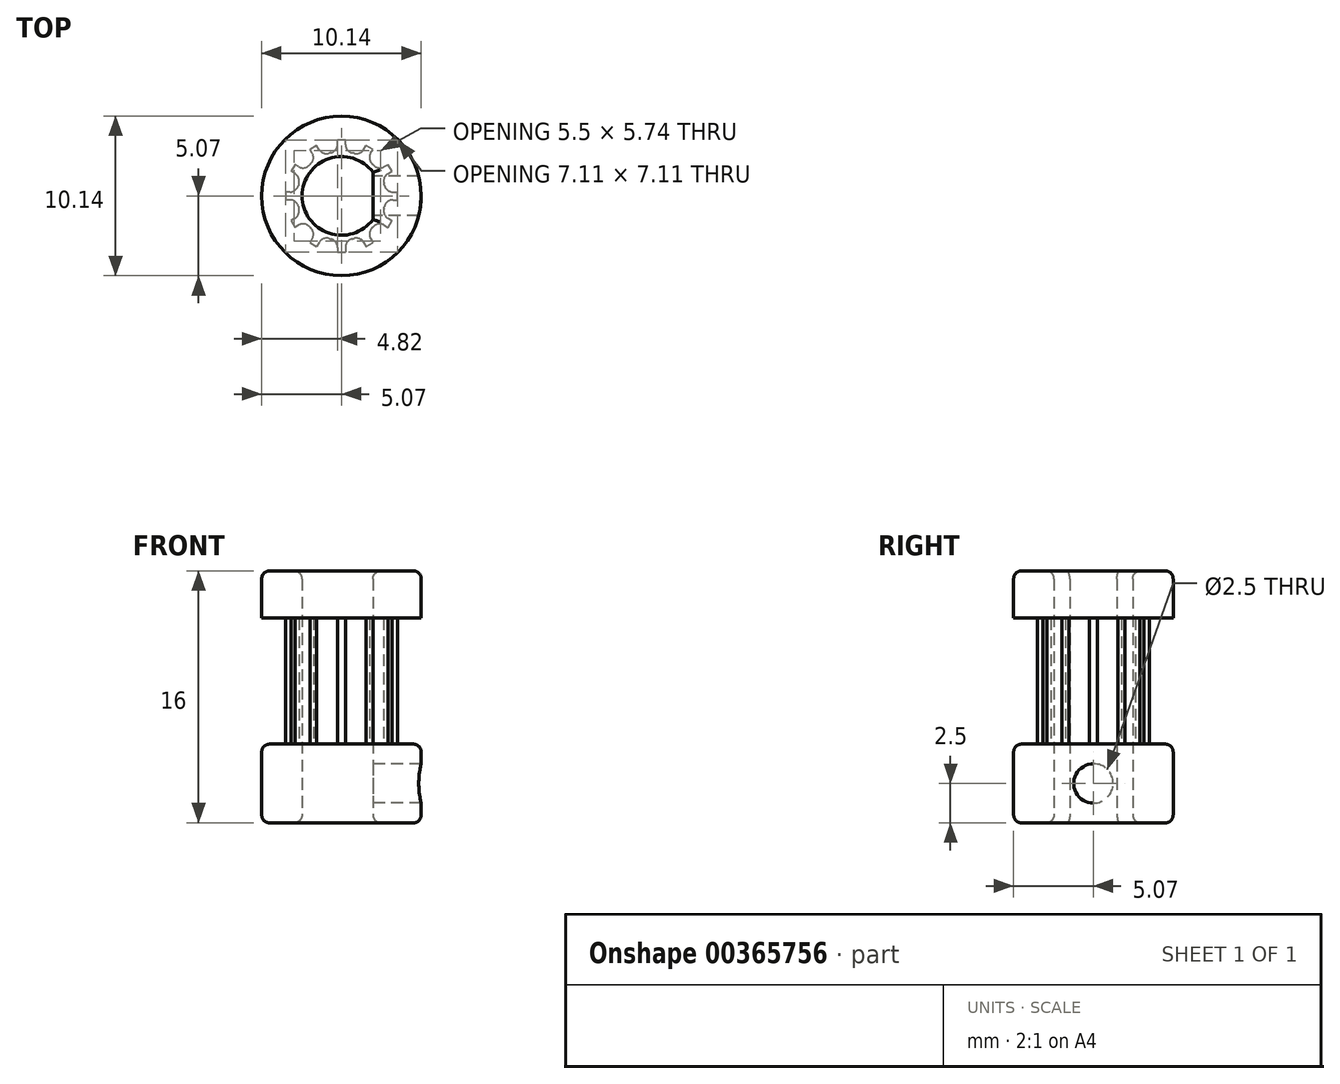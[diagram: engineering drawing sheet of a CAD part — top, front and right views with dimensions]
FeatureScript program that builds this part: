
annotation { "Feature Type Name" : "Feature", "Feature Type Description" : "" }
export const myFeature = defineFeature(function(context is Context, id is Id, definition is map)
    precondition{}
    {
        {
            assignVariable(context, id + "F0", {"name" : "Pulley_height", "anyValue" : 16});
        }
        {
            assignVariable(context, id + "F1", {"name" : "Belt_width", "anyValue" : 8});
        }
        {
            assignVariable(context, id + "F2", {"name" : "Nr_of_teeth", "anyValue" : 12});
        }
        {
            assignVariable(context, id + "F3", {"name" : "Top_sleeve_thickness", "anyValue" : 3});
        }
        {
            var Q0;
            Q0=qCreatedBy(makeId("Top.planeOp"),FACE);
            var sketch = newSketch(context, id + "F4", { "sketchPlane" : qUnion([Q0])});
            skCircle(sketch, "E0", {"center": v(0, 0) * mm, "radius": 3.57 * mm, "construction": true});
            skCircle(sketch, "E1", {"center": v(0, 0) * mm, "radius": 5.07 * mm});
            skLineSegment(sketch, "E2", {"start": v(0, -3.57) * mm, "end": v(0, 0) * mm, "construction": true});
            skLineSegment(sketch, "E3.bottom", {"start": v(-0.25, -2.8) * mm, "end": v(0.25, -2.8) * mm});
            skLineSegment(sketch, "E3.top", {"start": v(-0.25, -3.56) * mm, "end": v(0.25, -3.56) * mm});
            skLineSegment(sketch, "E3.left", {"start": v(-0.25, -3.27) * mm, "end": v(-0.25, -3.56) * mm});
            skLineSegment(sketch, "E3.right", {"start": v(0.25, -3.27) * mm, "end": v(0.25, -3.56) * mm});
            skPoint(sketch, "E3.middle", {"position": v(0, -3.18) * mm});
            skArc(sketch, "E4", {"start": v(0.67, -2.74) * mm, "mid": v(-0.21, 2.8) * mm, "end": v(-0.25, -2.8) * mm});
            skPoint(sketch, "E5.visualSharp", {"position": v(0.25, -2.8) * mm});
            skArc(sketch, "E5.filletArc", {"start": v(0.67, -2.74) * mm, "mid": v(0.37, -2.93) * mm, "end": v(0.25, -3.27) * mm});
            skArc(sketch, "E6.MirrorCS", {"start": v(-0.67, -2.74) * mm, "mid": v(-0.37, -2.93) * mm, "end": v(-0.25, -3.27) * mm});
            skLineSegment(sketch, "E7", {"start": v(0.67, -2.74) * mm, "end": v(0.25, -2.8) * mm});
            skCircle(sketch, "E8", {"center": v(0, 0) * mm, "radius": 2.5 * mm});
            skLineSegment(sketch, "E9", {"start": v(2, -1.5) * mm, "end": v(2, 1.5) * mm});
            skSolve(sketch);
        }
        {
            var Q0;
            {var subQ3=sQuery(id+"F4.wireOp",EDGE,"E3.bottom");Q0=makeQuery(id+"F4.imprint","IMPRINT",FACE,{"disambiguationData":[TD([[makeQuery(id+"F4.imprint","IMPRINT",EDGE,{"derivedFrom":subQ3}),1.0]])]});}
            var Q1;
            {var subQ0=sQuery(id+"F4.wireOp",EDGE,"c6fd6b1b-5dc8-40e9-8271-47284b0c1c390.MirrorCS");Q1=makeQuery(id+"F4.imprint","IMPRINT",FACE,{"disambiguationData":[TD([[makeQuery(id+"F4.imprint","IMPRINT",EDGE,{"derivedFrom":subQ0}),1.0]])]});}
            var Q2;
            {var subQ0=sQuery(id+"F4.wireOp",EDGE,"E9");Q2=makeQuery(id+"F4.imprint","IMPRINT",FACE,{"disambiguationData":[TD([[makeQuery(id+"F4.imprint","IMPRINT",EDGE,{"derivedFrom":subQ0}),-1.0]])]});}
            var Q3;
            Q3=makeQuery(id+"F4.imprint","IMPRINT",FACE,{"disambiguationData":[TD([[makeQuery(id+"F4.imprint","IMPRINT",EDGE,{"derivedFrom":sQuery(id+"F4.wireOp",EDGE,"E1")}),1.0]])]});
            var Q4;
            {var subQ0=sQuery(id+"F4.wireOp",EDGE,"E3.bottom");Q4=makeQuery(id+"F4.imprint","IMPRINT",FACE,{"disambiguationData":[TD([[makeQuery(id+"F4.imprint","IMPRINT",EDGE,{"derivedFrom":subQ0}),-1.0]])]});}
            extrude(context, id + "F5", {"entities" : qUnion([Q0, Q1, Q2, Q3, Q4]), "depth" : (getVariable(context, 'Pulley_height')) * mm});
        }
        {
            var Q0;
            Q0=makeQuery(id+"F4.imprint","IMPRINT",FACE,{"disambiguationData":[TD([[makeQuery(id+"F4.imprint","IMPRINT",EDGE,{"derivedFrom":sQuery(id+"F4.wireOp",EDGE,"E1")}),1.0]])]});
            var Q1;
            Q1=sQuery(id+"F4.wireOp",EDGE,"E1");
            extrude(context, id + "F6", {"entities" : qUnion([Q0]), "operationType" : NewBodyOperationType.REMOVE, "surfaceEntities" : qUnion([Q1]), "depth" : (getVariable(context, 'Pulley_height') - getVariable(context, 'Top_sleeve_thickness')) * mm});
        }
        {
            var Q0;
            Q0=makeQuery(id+"F4.imprint","IMPRINT",FACE,{"disambiguationData":[TD([[makeQuery(id+"F4.imprint","IMPRINT",EDGE,{"derivedFrom":sQuery(id+"F4.wireOp",EDGE,"E1")}),1.0]])]});
            extrude(context, id + "F7", {"entities" : qUnion([Q0]), "operationType" : NewBodyOperationType.ADD, "depth" : (getVariable(context, 'Pulley_height') - getVariable(context, 'Top_sleeve_thickness') - getVariable(context, 'Belt_width')) * mm});
        }
        {
            var Q0;
            Q0=qCreatedBy(makeId("Right.planeOp"),FACE);
            var sketch = newSketch(context, id + "F8", { "sketchPlane" : qUnion([Q0])});
            skCircle(sketch, "E10", {"center": v(0, 2.5) * mm, "radius": 1.25 * mm});
            skLineSegment(sketch, "E11", {"start": v(0, 0) * mm, "end": v(0, 16.5) * mm, "construction": true});
            skSolve(sketch);
        }
        {
            var Q0;
            Q0=makeQuery(id+"F8.imprint","IMPRINT",FACE,{"disambiguationData":[TD([[makeQuery(id+"F8.imprint","IMPRINT",EDGE,{"derivedFrom":sQuery(id+"F8.wireOp",EDGE,"E10")}),1.0]])]});
            var Q1;
            Q1=sQuery(id+"F8.wireOp",EDGE,"E10");
            extrude(context, id + "F9", {"entities" : qUnion([Q0]), "operationType" : NewBodyOperationType.REMOVE, "surfaceEntities" : qUnion([Q1]), "endBound" : BoundingType.THROUGH_ALL, "depth" : 25 * mm});
        }
        {
            var Q0;
            Q0=makeQuery(id+"F6.boolean.opBoolean","COPY",FACE,{"derivedFrom":makeQuery(id+"F6.opExtrude","SWEPT_FACE",FACE,{"disambiguationData":[OSD([sQuery(id+"F4.wireOp",EDGE,"E3.top")])]})});
            var Q1;
            Q1=makeQuery(id+"F6.boolean.opBoolean","COPY",FACE,{"derivedFrom":makeQuery(id+"F6.opExtrude","SWEPT_FACE",FACE,{"disambiguationData":[OSD([sQuery(id+"F4.wireOp",EDGE,"E6.MirrorCS")])]})});
            var Q2;
            Q2=makeQuery(id+"F6.boolean.opBoolean","COPY",FACE,{"derivedFrom":makeQuery(id+"F6.opExtrude","SWEPT_FACE",FACE,{"disambiguationData":[OSD([sQuery(id+"F4.wireOp",EDGE,"E5.filletArc")])]})});
            var Q3;
            Q3=makeQuery(id+"F6.boolean.opBoolean","COPY",FACE,{"derivedFrom":makeQuery(id+"F6.opExtrude","SWEPT_FACE",FACE,{"disambiguationData":[OSD([sQuery(id+"F4.wireOp",EDGE,"E3.left")])]})});
            var Q4;
            Q4=makeQuery(id+"F6.boolean.opBoolean","COPY",FACE,{"derivedFrom":makeQuery(id+"F6.opExtrude","SWEPT_FACE",FACE,{"disambiguationData":[OSD([sQuery(id+"F4.wireOp",EDGE,"E3.right")])]})});
            var Q5;
            Q5=sQuery(id+"F8.wireOp",EDGE,"E11");
            circularPattern(context, id + "F10", {"patternType" : PatternType.FACE, "operationType" : NewBodyOperationType.ADD, "faces" : qUnion([Q0, Q1, Q2, Q3, Q4]), "axis" : qUnion([Q5]), "angle" : 360 * degree, "instanceCount" : getVariable(context, 'Nr_of_teeth'), "equalSpace" : true});
        }
        {
            var Q0;
            Q0=makeQuery(id+"F6.boolean.opBoolean","COPY",EDGE,{"derivedFrom":makeQuery(id+"F6.opExtrude","CAP_EDGE",EDGE,{"disambiguationData":[OSD([sQuery(id+"F4.wireOp",EDGE,"E1")])],"isStart":false})});
            var Q1;
            Q1=makeQuery(id+"F5.opExtrude","CAP_EDGE",EDGE,{"disambiguationData":[OSD([sQuery(id+"F4.wireOp",EDGE,"E1")])],"isStart":false});
            var Q2;
            Q2=makeQuery(id+"F7.opExtrude","CAP_EDGE",EDGE,{"disambiguationData":[OSD([sQuery(id+"F4.wireOp",EDGE,"E1")])],"isStart":false});
            var Q3;
            Q3=makeQuery(id+"F7.opExtrude","CAP_EDGE",EDGE,{"disambiguationData":[OSD([sQuery(id+"F4.wireOp",EDGE,"E1")])],"isStart":true});
            var Q4;
            Q4=makeQuery(id+"F5.opExtrude","CAP_EDGE",EDGE,{"disambiguationData":[OSD([sQuery(id+"F4.wireOp",EDGE,"E8")])],"isStart":false});
            var Q5;
            Q5=makeQuery(id+"F5.opExtrude","CAP_EDGE",EDGE,{"disambiguationData":[OSD([sQuery(id+"F4.wireOp",EDGE,"E8")])],"isStart":true});
            var Q6;
            Q6=makeQuery(id+"F5.opExtrude","CAP_EDGE",EDGE,{"disambiguationData":[OSD([sQuery(id+"F4.wireOp",EDGE,"E9")])],"isStart":true});
            var Q7;
            Q7=makeQuery(id+"F5.opExtrude","CAP_EDGE",EDGE,{"disambiguationData":[OSD([sQuery(id+"F4.wireOp",EDGE,"E9")])],"isStart":false});
            fillet(context, id + "F11", {"entities" : qUnion([Q0, Q1, Q2, Q3, Q4, Q5, Q6, Q7]), "radius" : 0.5 * mm, "tangentPropagation" : true, "allowEdgeOverflow" : false});
        }
    });
